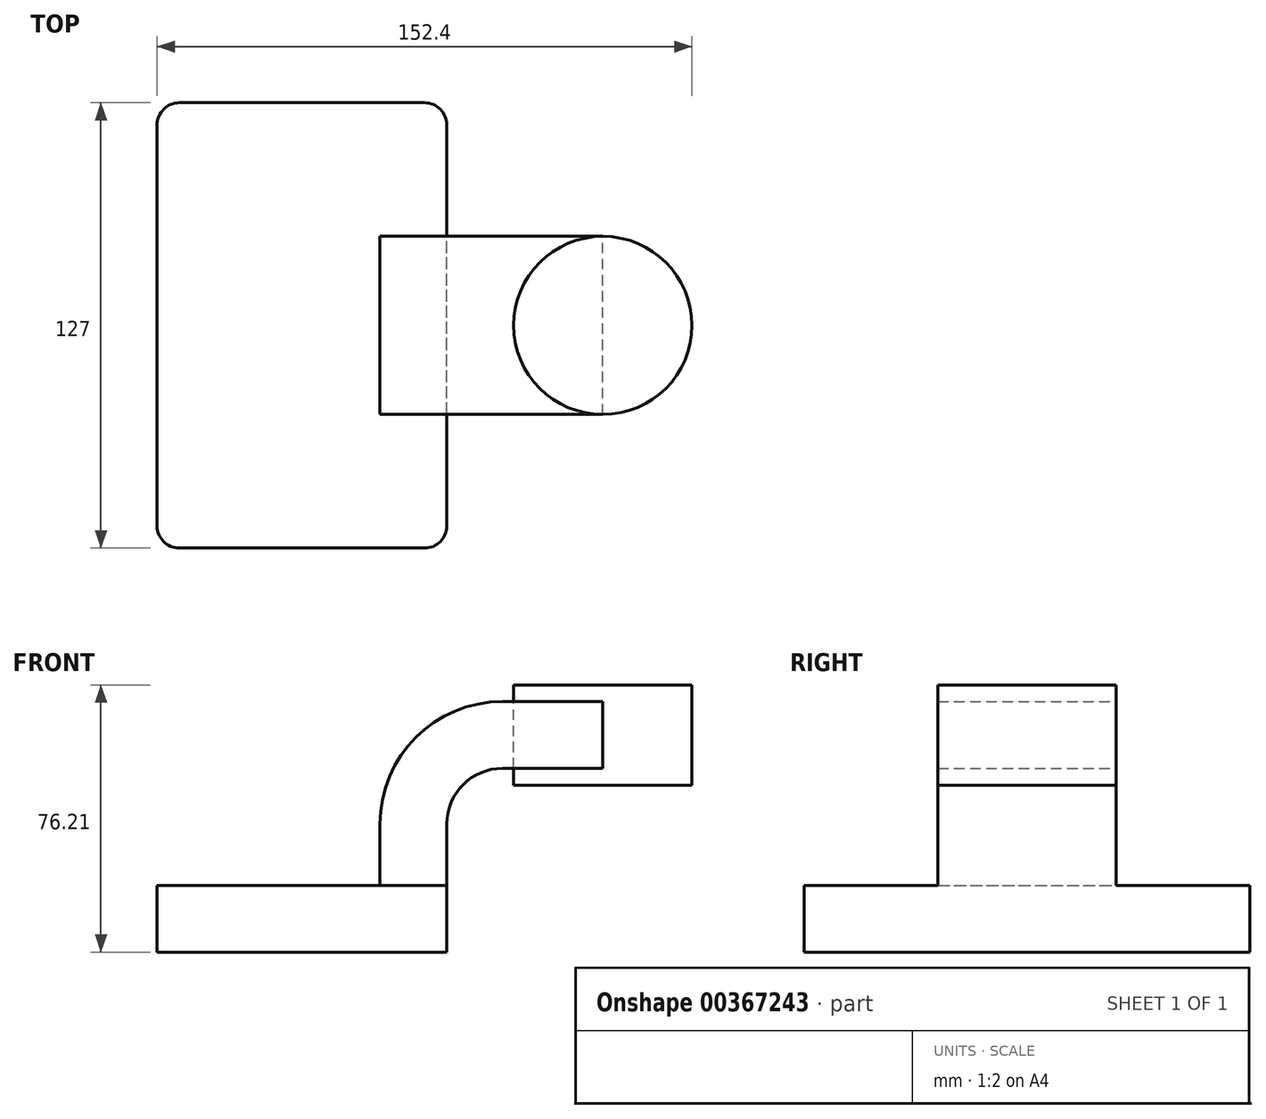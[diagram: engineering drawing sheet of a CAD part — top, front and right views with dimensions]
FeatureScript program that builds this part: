
annotation { "Feature Type Name" : "Feature", "Feature Type Description" : "" }
export const myFeature = defineFeature(function(context is Context, id is Id, definition is map)
    precondition{}
    {
        {
            var Q0;
            Q0=qCreatedBy(makeId("Front.planeOp"),FACE);
            var sketch = newSketch(context, id + "F0", { "sketchPlane" : qUnion([Q0])});
            skLineSegment(sketch, "E0.bottom", {"start": v(41.28, -9.52) * mm, "end": v(-41.27, -9.53) * mm});
            skLineSegment(sketch, "E0.top", {"start": v(41.27, 9.53) * mm, "end": v(-41.28, 9.53) * mm});
            skLineSegment(sketch, "E0.left", {"start": v(41.28, -9.52) * mm, "end": v(41.28, 9.53) * mm});
            skLineSegment(sketch, "E0.right", {"start": v(-41.27, -9.52) * mm, "end": v(-41.28, 9.53) * mm});
            skPoint(sketch, "E0.middle", {"position": v(0, 0) * mm});
            skLineSegment(sketch, "E1.bottom", {"start": v(111.12, 38.1) * mm, "end": v(60.32, 38.1) * mm});
            skLineSegment(sketch, "E1.top", {"start": v(111.12, 66.68) * mm, "end": v(60.32, 66.68) * mm});
            skLineSegment(sketch, "E1.left", {"start": v(111.12, 38.1) * mm, "end": v(111.12, 66.68) * mm});
            skLineSegment(sketch, "E1.right", {"start": v(60.32, 38.1) * mm, "end": v(60.32, 66.68) * mm});
            skPoint(sketch, "E1.middle", {"position": v(85.72, 52.39) * mm});
            skLineSegment(sketch, "E2", {"start": v(41.27, 9.53) * mm, "end": v(41.27, 27) * mm});
            skArc(sketch, "E3", {"start": v(41.27, 27) * mm, "mid": v(45.92, 38.23) * mm, "end": v(57.15, 42.88) * mm});
            skLineSegment(sketch, "E4", {"start": v(57.15, 42.88) * mm, "end": v(85.73, 42.88) * mm});
            skLineSegment(sketch, "E5.0", {"start": v(57.15, 61.93) * mm, "end": v(85.72, 61.93) * mm});
            skArc(sketch, "E5.1", {"start": v(22.23, 27) * mm, "mid": v(32.45, 51.7) * mm, "end": v(57.15, 61.93) * mm});
            skLineSegment(sketch, "E5.2", {"start": v(22.23, 9.53) * mm, "end": v(22.23, 27) * mm});
            skLineSegment(sketch, "E6", {"start": v(85.73, 42.88) * mm, "end": v(85.73, 61.93) * mm});
            skFitSpline(sketch, "E7", {"points": [v(57.15, 61.93) * mm, v(-41.28, 9.53) * mm], "startDerivative": vector(-105.1, 0.34) * mm, "endDerivative": vector(0.15, -71.02) * mm});
            skPoint(sketch, "E8", {"position": v(85.72, 66.68) * mm});
            skLineSegment(sketch, "E9", {"start": v(85.72, 66.68) * mm, "end": v(85.72, 38.1) * mm});
            skSolve(sketch);
        }
        {
            var Q0;
            Q0=makeQuery(id+"F0.imprint","IMPRINT",FACE,{"disambiguationData":[TD([[makeQuery(id+"F0.imprint","IMPRINT",EDGE,{"derivedFrom":sQuery(id+"F0.wireOp",EDGE,"E0.bottom")}),-1.0]])]});
            extrude(context, id + "F1", {"entities" : qUnion([Q0]), "endBound" : BoundingType.SYMMETRIC, "depth" : 127 * mm});
        }
        {
            var Q0;
            {var subQ1=sQuery(id+"F0.wireOp",EDGE,"E2");Q0=makeQuery(id+"F0.imprint","IMPRINT",FACE,{"disambiguationData":[TD([[makeQuery(id+"F0.imprint","IMPRINT",EDGE,{"derivedFrom":subQ1}),1.0]])]});}
            var Q1;
            {var subQ5=sQuery(id+"F0.wireOp",EDGE,"E6");Q1=makeQuery(id+"F0.imprint","IMPRINT",FACE,{"disambiguationData":[TD([[makeQuery(id+"F0.imprint","IMPRINT",EDGE,{"derivedFrom":subQ5}),1.0]])]});}
            var Q2;
            {var subQ0=sQuery(id+"F0.wireOp",EDGE,"E4");var subQ1=sQuery(id+"F0.wireOp",EDGE,"E1.right");var subQ2=makeQuery(id+"F0.imprint","INTERSECT",VERTEX,{"derivedFrom":[subQ1,subQ0]});Q2=makeQuery(id+"F0.imprint","IMPRINT",FACE,{"disambiguationData":[TD([[makeQuery(id+"F0.imprint","IMPRINT",EDGE,{"disambiguationData":[TD([[subQ2,-1.0]])],"derivedFrom":subQ1}),-1.0]])]});}
            extrude(context, id + "F2", {"entities" : qUnion([Q0, Q1, Q2]), "operationType" : NewBodyOperationType.ADD, "endBound" : BoundingType.SYMMETRIC, "depth" : 50.8 * mm});
        }
        {
            var Q0;
            Q0=makeQuery(id+"F0.imprint","IMPRINT",FACE,{"disambiguationData":[TD([[makeQuery(id+"F0.imprint","IMPRINT",EDGE,{"derivedFrom":sQuery(id+"F0.wireOp",EDGE,"E5.1")}),1.0]])]});
            extrude(context, id + "F3", {"entities" : qUnion([Q0]), "operationType" : NewBodyOperationType.ADD, "endBound" : BoundingType.SYMMETRIC, "depth" : 15.88 * mm});
        }
        {
            var Q0;
            {var subQ0=sQuery(id+"F0.wireOp",EDGE,"E1.left");Q0=makeQuery(id+"F0.imprint","IMPRINT",FACE,{"disambiguationData":[TD([[makeQuery(id+"F0.imprint","IMPRINT",EDGE,{"derivedFrom":subQ0}),1.0]])]});}
            var Q1;
            Q1=sQuery(id+"F0.wireOp",EDGE,"E9");
            revolve(context, id + "F4", {"entities" : qUnion([Q0]), "axis" : qUnion([Q1]), "revolveType" : RevolveType.FULL});
        }
        {
            var Q0;
            Q0=makeQuery(id+"F1.opExtrude","CAP_EDGE",EDGE,{"disambiguationData":[OSD([sQuery(id+"F0.wireOp",EDGE,"E0.left")])],"isStart":false});
            var Q1;
            Q1=makeQuery(id+"F1.opExtrude","CAP_EDGE",EDGE,{"disambiguationData":[OSD([sQuery(id+"F0.wireOp",EDGE,"E0.right")])],"isStart":false});
            var Q2;
            Q2=makeQuery(id+"F1.opExtrude","CAP_EDGE",EDGE,{"disambiguationData":[OSD([sQuery(id+"F0.wireOp",EDGE,"E0.right")])],"isStart":true});
            var Q3;
            Q3=makeQuery(id+"F1.opExtrude","CAP_EDGE",EDGE,{"disambiguationData":[OSD([sQuery(id+"F0.wireOp",EDGE,"E0.left")])],"isStart":true});
            fillet(context, id + "F5", {"entities" : qUnion([Q0, Q1, Q2, Q3]), "radius" : 6.35 * mm, "tangentPropagation" : true, "allowEdgeOverflow" : false});
        }
    });
